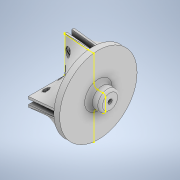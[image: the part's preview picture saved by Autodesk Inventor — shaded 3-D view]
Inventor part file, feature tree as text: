
AUTODESK INVENTOR PART (.ipt)
format: ipt  version: 2022 (Build 260153000, 153)  size: 571,392 bytes
history: native  units: mm
features: other x6, sketch x5, extrude x4, projected_geometry x4, pattern_circular x1, fillet x1
ambient origin geometry x8: Origin, YZ Plane, XZ Plane, XY Plane, X Axis, Y Axis, Z Axis, Center Point
bodies: Body1 (feature_tree)
feature tree (21):
  other  "Твердое тело2"
  other  "Исправленная геометрия1"
  other  "РабПлоскость1"
  extrude  "Выдавливание1"  [1 undecoded]
  other  "РабПлоскость2"
  extrude  "Выдавливание2"  Depth=22.5mm
  extrude  "Выдавливание3"  Depth=17.5mm
  pattern_circular  "Круговой массив1"  [2 undecoded]
  other  "РабПлоскость3"
  extrude  "Выдавливание4"  Depth=20.0mm
  fillet  "Сопряжение2"  Radius=12.0mm
  sketch  "Эскиз8"
  sketch  "Эскиз1"
  sketch  "Эскиз2"
  projected_geometry  "Спроецированная петля1"
  projected_geometry  "Спроецированная петля2"
  sketch  "Эскиз3"
  projected_geometry  "Спроецированная петля3"
  projected_geometry  "Спроецированная петля4"
  sketch  "Эскиз4"
  other  "Твердое тело1"
note: 3 required parameter values undecoded (feature->parameter linkage not recoverable at this tier; creation-order binding heuristic only, values carry confidence <= 0.55)
